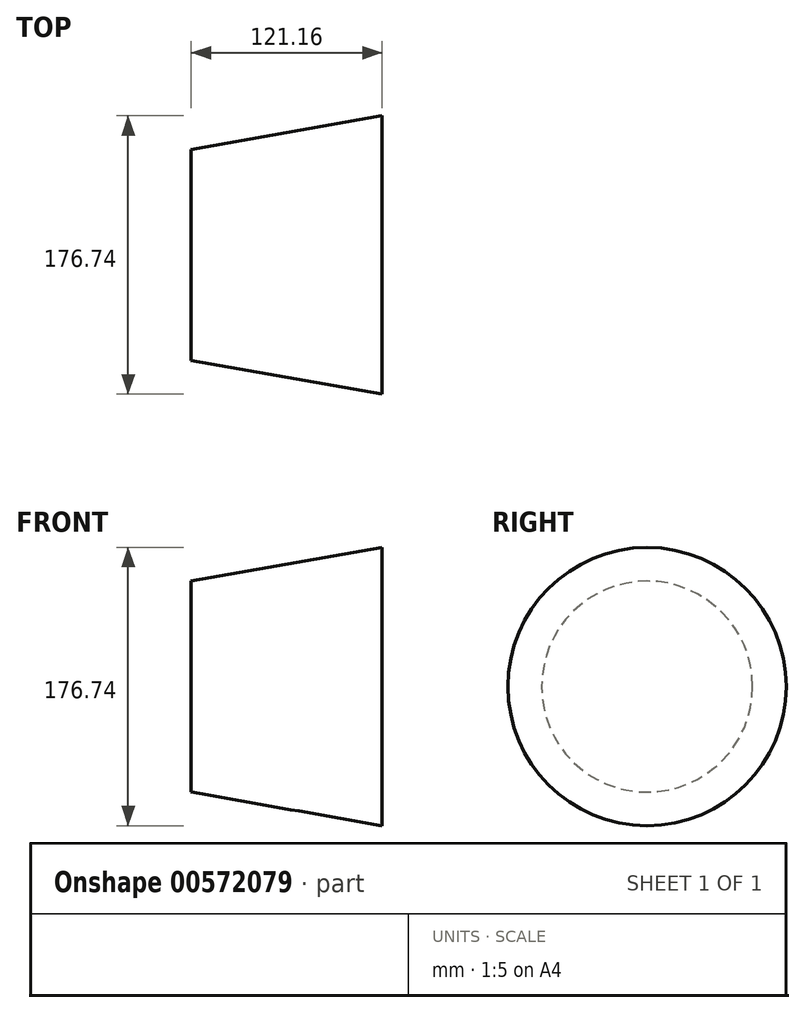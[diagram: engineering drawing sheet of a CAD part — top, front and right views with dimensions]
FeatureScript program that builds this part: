
annotation { "Feature Type Name" : "Feature", "Feature Type Description" : "" }
export const myFeature = defineFeature(function(context is Context, id is Id, definition is map)
    precondition{}
    {
        {
            var Q0;
            Q0=qCreatedBy(makeId("Right.planeOp"),FACE);
            var sketch = newSketch(context, id + "F0", { "sketchPlane" : qUnion([Q0])});
            skCircle(sketch, "E0", {"center": v(-99.27, 13.29) * mm, "radius": 67 * mm});
            skSolve(sketch);
        }
        {
            var Q0;
            Q0=makeQuery(id+"F0.imprint","IMPRINT",FACE,{"disambiguationData":[TD([[makeQuery(id+"F0.imprint","IMPRINT",EDGE,{"derivedFrom":sQuery(id+"F0.wireOp",EDGE,"E0")}),1.0]])]});
            extrude(context, id + "F1", {"entities" : qUnion([Q0]), "depth" : 121.16 * mm, "offsetDistance" : 25.4 * mm, "hasDraft" : true, "draftAngle" : 10 * degree});
        }
    });
